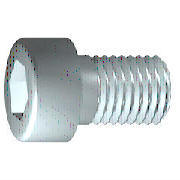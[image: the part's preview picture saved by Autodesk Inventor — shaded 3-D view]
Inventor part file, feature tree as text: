
AUTODESK INVENTOR PART (.ipt)
format: ipt  version: 2019 (Build 230136000, 136)  size: 194,048 bytes
history: native  units: mm (DEFAULTED — no unit token found)
features: sketch x2, extrude x1, plane x1, fillet x1
ambient origin geometry x7: Origin, YZ Plane, XY Plane, X Axis, Y Axis, Z Axis, Center Point
bodies: Solid1 (feature_tree), Body (feature_tree)
feature tree (5):
  extrude  "Slot"  Depth=3.0mm
  plane  "Work Plane1"
  fillet  "Fillet2"  Radius=3.0mm
  sketch  "Sketch1"  dims[d1=4.75mm d2=0.306825mm d3=3.0mm]
  sketch  "Sketch2"  dims[d4=1.3mm d5=60.0deg d6=3.0mm d7=3.0mm d8=2.886751mm d9=5.5mm d10=90.0deg d11=10.0mm d12=0.0mm d13=4.75mm d14=0.0mm d15=0.306725mm d16=0.306725mm d17=0.3mm d19=0.0mm d26=6.0mm d27=45.0deg d28=0.0mm d29=0.0mm d30=0.1mm]
